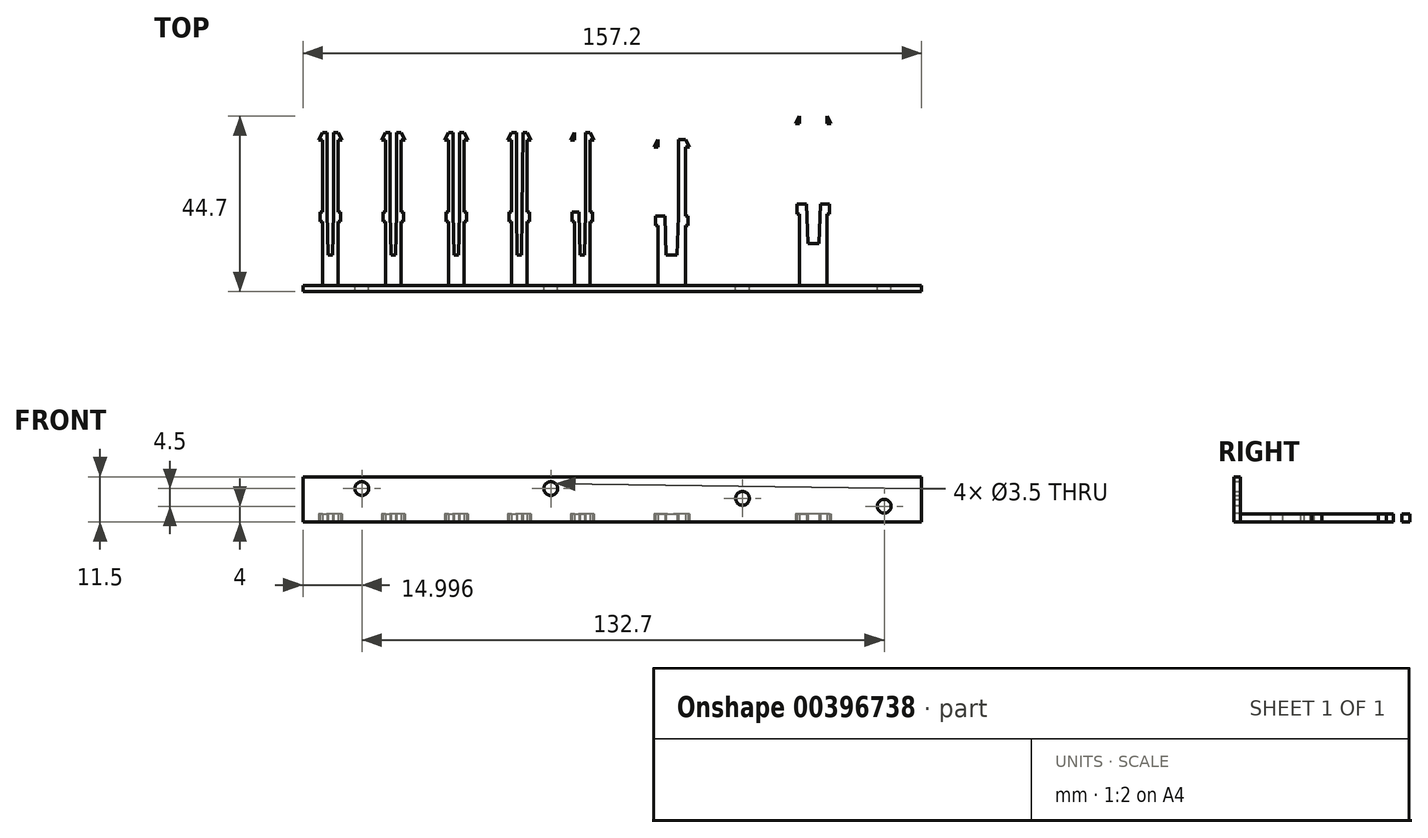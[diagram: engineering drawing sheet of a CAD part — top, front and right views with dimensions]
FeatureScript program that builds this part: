
annotation { "Feature Type Name" : "Feature", "Feature Type Description" : "" }
export const myFeature = defineFeature(function(context is Context, id is Id, definition is map)
    precondition{}
    {
        {
            var Q0;
            Q0=qCreatedBy(makeId("Top.planeOp"),FACE);
            var sketch = newSketch(context, id + "F0", { "sketchPlane" : qUnion([Q0])});
            skLineSegment(sketch, "E0.bottom", {"start": v(0.4, 5.8) * mm, "end": v(21.9, 5.8) * mm});
            skLineSegment(sketch, "E0.top", {"start": v(0.4, -4.9) * mm, "end": v(21.9, -4.9) * mm});
            skLineSegment(sketch, "E0.left", {"start": v(0.4, 5.8) * mm, "end": v(0.4, -4.9) * mm});
            skLineSegment(sketch, "E0.right", {"start": v(21.9, 5.8) * mm, "end": v(21.9, -4.9) * mm});
            skLineSegment(sketch, "E1.top", {"start": v(0.4, -7.9) * mm, "end": v(21.9, -7.9) * mm});
            skLineSegment(sketch, "E1.left", {"start": v(0.4, -4.9) * mm, "end": v(0.4, -7.9) * mm});
            skLineSegment(sketch, "E1.right", {"start": v(21.9, -4.9) * mm, "end": v(21.9, -7.9) * mm});
            skLineSegment(sketch, "E2.bottom", {"start": v(21.9, -7.9) * mm, "end": v(24.9, -7.9) * mm});
            skLineSegment(sketch, "E2.top", {"start": v(21.9, 8.8) * mm, "end": v(24.9, 8.8) * mm});
            skLineSegment(sketch, "E2.left", {"start": v(21.9, -7.9) * mm, "end": v(21.9, 8.8) * mm});
            skLineSegment(sketch, "E2.right", {"start": v(24.9, -7.9) * mm, "end": v(24.9, 8.8) * mm});
            skLineSegment(sketch, "E3", {"start": v(21.9, 8.8) * mm, "end": v(20.1, 5.8) * mm});
            skLineSegment(sketch, "E4.MirrorCS", {"start": v(0.4, -4.9) * mm, "end": v(-21.1, -4.9) * mm});
            skLineSegment(sketch, "E5.MirrorCS", {"start": v(-21.1, -7.9) * mm, "end": v(-21.1, 8.8) * mm});
            skLineSegment(sketch, "E6.MirrorCS", {"start": v(0.4, 5.8) * mm, "end": v(-21.1, 5.8) * mm});
            skLineSegment(sketch, "E7.MirrorCS", {"start": v(-21.1, 8.8) * mm, "end": v(-19.3, 5.8) * mm});
            skLineSegment(sketch, "E8.MirrorCS", {"start": v(-21.1, 8.8) * mm, "end": v(-24.1, 8.8) * mm});
            skLineSegment(sketch, "E9.MirrorCS", {"start": v(-24.1, -7.9) * mm, "end": v(-24.1, 8.8) * mm});
            skLineSegment(sketch, "E10.MirrorCS", {"start": v(0.4, -7.9) * mm, "end": v(-21.1, -7.9) * mm});
            skLineSegment(sketch, "E11.MirrorCS", {"start": v(-21.1, -7.9) * mm, "end": v(-24.1, -7.9) * mm});
            skLineSegment(sketch, "E12.bottom", {"start": v(0.4, -6.4) * mm, "end": v(3.4, -6.4) * mm});
            skLineSegment(sketch, "E12.top", {"start": v(0.4, -7.9) * mm, "end": v(3.4, -7.9) * mm});
            skLineSegment(sketch, "E12.left", {"start": v(0.4, -6.4) * mm, "end": v(0.4, -7.9) * mm});
            skLineSegment(sketch, "E12.right", {"start": v(3.4, -6.4) * mm, "end": v(3.4, -7.9) * mm});
            skLineSegment(sketch, "E13.MirrorCS", {"start": v(0.4, -6.4) * mm, "end": v(-2.6, -6.4) * mm});
            skLineSegment(sketch, "E14.MirrorCS", {"start": v(-2.6, -6.4) * mm, "end": v(-2.6, -7.9) * mm});
            skLineSegment(sketch, "E15.bottom", {"start": v(-24.1, -7.9) * mm, "end": v(-24.7, -7.9) * mm});
            skLineSegment(sketch, "E15.top", {"start": v(-24.1, -4.9) * mm, "end": v(-24.7, -4.9) * mm});
            skLineSegment(sketch, "E15.left", {"start": v(-24.1, -7.9) * mm, "end": v(-24.1, -4.9) * mm});
            skLineSegment(sketch, "E15.right", {"start": v(-24.7, -7.9) * mm, "end": v(-24.7, -4.9) * mm});
            skLineSegment(sketch, "E16.MirrorCS", {"start": v(-49.8, -4.9) * mm, "end": v(-49.8, -7.9) * mm});
            skLineSegment(sketch, "E17.MirrorCS", {"start": v(-49.8, -6.4) * mm, "end": v(-49.8, -7.9) * mm});
            skLineSegment(sketch, "E18.MirrorCS", {"start": v(-52.8, -6.4) * mm, "end": v(-52.8, -7.9) * mm});
            skLineSegment(sketch, "E19.MirrorCS", {"start": v(-46.8, -6.4) * mm, "end": v(-46.8, -7.9) * mm});
            skLineSegment(sketch, "E20.MirrorCS", {"start": v(-49.8, -4.9) * mm, "end": v(-71.3, -4.9) * mm});
            skLineSegment(sketch, "E21.MirrorCS", {"start": v(-71.3, 5.8) * mm, "end": v(-71.3, -4.9) * mm});
            skLineSegment(sketch, "E22.MirrorCS", {"start": v(-49.8, -6.4) * mm, "end": v(-52.8, -6.4) * mm});
            skLineSegment(sketch, "E23.MirrorCS", {"start": v(-71.3, -4.9) * mm, "end": v(-71.3, -7.9) * mm});
            skLineSegment(sketch, "E24.MirrorCS", {"start": v(-71.3, -7.9) * mm, "end": v(-74.3, -7.9) * mm});
            skLineSegment(sketch, "E25.MirrorCS", {"start": v(-49.8, -7.9) * mm, "end": v(-28.3, -7.9) * mm});
            skLineSegment(sketch, "E26.MirrorCS", {"start": v(-49.8, -7.9) * mm, "end": v(-52.8, -7.9) * mm});
            skLineSegment(sketch, "E27.MirrorCS", {"start": v(-49.8, -4.9) * mm, "end": v(-28.3, -4.9) * mm});
            skLineSegment(sketch, "E28.MirrorCS", {"start": v(-28.3, -7.9) * mm, "end": v(-28.3, 8.8) * mm});
            skLineSegment(sketch, "E29.MirrorCS", {"start": v(-49.8, 5.8) * mm, "end": v(-28.3, 5.8) * mm});
            skLineSegment(sketch, "E30.MirrorCS", {"start": v(-49.8, 5.8) * mm, "end": v(-71.3, 5.8) * mm});
            skLineSegment(sketch, "E31.MirrorCS", {"start": v(-28.3, 8.8) * mm, "end": v(-30.1, 5.8) * mm});
            skLineSegment(sketch, "E32.MirrorCS", {"start": v(-49.8, 5.8) * mm, "end": v(-49.8, -4.9) * mm});
            skLineSegment(sketch, "E33.MirrorCS", {"start": v(-49.8, -6.4) * mm, "end": v(-46.8, -6.4) * mm});
            skLineSegment(sketch, "E34.MirrorCS", {"start": v(-49.8, -7.9) * mm, "end": v(-71.3, -7.9) * mm});
            skLineSegment(sketch, "E35.MirrorCS", {"start": v(-28.3, -7.9) * mm, "end": v(-25.3, -7.9) * mm});
            skLineSegment(sketch, "E36.MirrorCS", {"start": v(-71.3, 8.8) * mm, "end": v(-74.3, 8.8) * mm});
            skLineSegment(sketch, "E37.MirrorCS", {"start": v(-71.3, -7.9) * mm, "end": v(-71.3, 8.8) * mm});
            skLineSegment(sketch, "E38.MirrorCS", {"start": v(-71.3, 8.8) * mm, "end": v(-69.5, 5.8) * mm});
            skLineSegment(sketch, "E39.MirrorCS", {"start": v(-28.3, 8.8) * mm, "end": v(-25.3, 8.8) * mm});
            skLineSegment(sketch, "E40.MirrorCS", {"start": v(-74.3, -7.9) * mm, "end": v(-74.3, 8.8) * mm});
            skLineSegment(sketch, "E41.MirrorCS", {"start": v(-25.3, -7.9) * mm, "end": v(-25.3, 8.8) * mm});
            skLineSegment(sketch, "E42.MirrorCS", {"start": v(-25.3, -4.9) * mm, "end": v(-24.7, -4.9) * mm});
            skLineSegment(sketch, "E43.MirrorCS", {"start": v(-25.3, -7.9) * mm, "end": v(-24.7, -7.9) * mm});
            skSolve(sketch);
        }
        {
            var Q0;
            Q0=qCreatedBy(makeId("Top.planeOp"),FACE);
            var sketch = newSketch(context, id + "F1", { "sketchPlane" : qUnion([Q0])});
            skLineSegment(sketch, "E44.bottom", {"start": v(-12.9, 18.7) * mm, "end": v(-10.9, 18.7) * mm});
            skLineSegment(sketch, "E44.top", {"start": v(-12.9, 0) * mm, "end": v(-10.9, 0) * mm});
            skLineSegment(sketch, "E44.left", {"start": v(-12.9, 18.7) * mm, "end": v(-12.9, 0) * mm});
            skLineSegment(sketch, "E44.right", {"start": v(-10.9, 18.7) * mm, "end": v(-10.9, 0) * mm});
            skLineSegment(sketch, "E45.bottom", {"start": v(-81.9, 0) * mm, "end": v(75.3, 0) * mm});
            skLineSegment(sketch, "E45.top", {"start": v(-81.9, -1.6) * mm, "end": v(75.3, -1.6) * mm});
            skLineSegment(sketch, "E45.left", {"start": v(-81.9, 0) * mm, "end": v(-81.9, -1.6) * mm});
            skLineSegment(sketch, "E45.right", {"start": v(75.3, 0) * mm, "end": v(75.3, -1.6) * mm});
            skLineSegment(sketch, "E46.top", {"start": v(-11.5, 7.7) * mm, "end": v(-10.9, 7.7) * mm});
            skLineSegment(sketch, "E47", {"start": v(-13.5, 16.2) * mm, "end": v(-12.9, 16.2) * mm});
            skLineSegment(sketch, "E48.MirrorCS", {"start": v(-10.3, 7.7) * mm, "end": v(-10.9, 7.7) * mm});
            skLineSegment(sketch, "E49.MirrorCS", {"start": v(-8.9, 18.7) * mm, "end": v(-8.9, 0) * mm});
            skLineSegment(sketch, "E50.MirrorCS", {"start": v(-8.3, 16.2) * mm, "end": v(-8.9, 16.2) * mm});
            skLineSegment(sketch, "E51.MirrorCS", {"start": v(-8.9, 18.7) * mm, "end": v(-10.9, 18.7) * mm});
            skLineSegment(sketch, "E52", {"start": v(-11.5, 7.7) * mm, "end": v(-11.7, 18.7) * mm});
            skLineSegment(sketch, "E53.MirrorCS", {"start": v(-10.3, 7.7) * mm, "end": v(-10.1, 18.7) * mm});
            skLineSegment(sketch, "E54.bottom", {"start": v(8.3, 17.7) * mm, "end": v(11.8, 17.7) * mm});
            skLineSegment(sketch, "E54.left", {"start": v(8.3, 17.7) * mm, "end": v(8.3, 0) * mm});
            skLineSegment(sketch, "E54.right", {"start": v(11.8, 17.7) * mm, "end": v(11.8, -1.3) * mm});
            skLineSegment(sketch, "E55.top", {"start": v(10.4, 7.7) * mm, "end": v(11.8, 7.7) * mm});
            skLineSegment(sketch, "E56", {"start": v(7.7, 15.2) * mm, "end": v(8.3, 15.2) * mm});
            skLineSegment(sketch, "E57.MirrorCS", {"start": v(13.2, 7.7) * mm, "end": v(11.8, 7.7) * mm});
            skLineSegment(sketch, "E58.MirrorCS", {"start": v(15.3, 17.7) * mm, "end": v(15.3, 0) * mm});
            skLineSegment(sketch, "E59.MirrorCS", {"start": v(15.9, 15.2) * mm, "end": v(15.3, 15.2) * mm});
            skLineSegment(sketch, "E60.MirrorCS", {"start": v(15.3, 17.7) * mm, "end": v(11.8, 17.7) * mm});
            skLineSegment(sketch, "E61", {"start": v(10.4, 7.7) * mm, "end": v(10.06, 17.7) * mm});
            skLineSegment(sketch, "E62.MirrorCS", {"start": v(13.2, 7.7) * mm, "end": v(13.56, 17.7) * mm});
            skLineSegment(sketch, "E63.bottom", {"start": v(44.3, 20.7) * mm, "end": v(47.8, 20.7) * mm});
            skLineSegment(sketch, "E63.left", {"start": v(44.3, 20.7) * mm, "end": v(44.3, 0) * mm});
            skLineSegment(sketch, "E63.right", {"start": v(47.8, 20.7) * mm, "end": v(47.8, -1.3) * mm});
            skLineSegment(sketch, "E64.top", {"start": v(46.4, 10.7) * mm, "end": v(47.8, 10.7) * mm});
            skLineSegment(sketch, "E65", {"start": v(43.7, 18.2) * mm, "end": v(44.3, 18.2) * mm});
            skLineSegment(sketch, "E66.MirrorCS", {"start": v(49.2, 10.7) * mm, "end": v(47.8, 10.7) * mm});
            skLineSegment(sketch, "E67.MirrorCS", {"start": v(51.3, 20.7) * mm, "end": v(51.3, 0) * mm});
            skLineSegment(sketch, "E68.MirrorCS", {"start": v(51.3, 20.7) * mm, "end": v(47.8, 20.7) * mm});
            skLineSegment(sketch, "E69", {"start": v(46.4, 10.7) * mm, "end": v(46.06, 20.7) * mm});
            skLineSegment(sketch, "E70.MirrorCS", {"start": v(49.2, 10.7) * mm, "end": v(49.56, 20.7) * mm});
            skLineSegment(sketch, "E71.top", {"start": v(-28.9, 0) * mm, "end": v(-26.9, 0) * mm});
            skLineSegment(sketch, "E71.left", {"start": v(-28.9, 18.7) * mm, "end": v(-28.9, 0) * mm});
            skLineSegment(sketch, "E71.right", {"start": v(-26.9, 18.7) * mm, "end": v(-26.9, 0) * mm});
            skLineSegment(sketch, "E72.top", {"start": v(-27.5, 7.7) * mm, "end": v(-26.9, 7.7) * mm});
            skLineSegment(sketch, "E73.MirrorCS", {"start": v(-26.3, 7.7) * mm, "end": v(-26.9, 7.7) * mm});
            skLineSegment(sketch, "E74.MirrorCS", {"start": v(-24.9, 18.7) * mm, "end": v(-24.9, 0) * mm});
            skLineSegment(sketch, "E75.MirrorCS", {"start": v(-24.3, 16.2) * mm, "end": v(-24.9, 16.2) * mm});
            skLineSegment(sketch, "E76.MirrorCS", {"start": v(-24.9, 18.7) * mm, "end": v(-26.9, 18.7) * mm});
            skLineSegment(sketch, "E77", {"start": v(-27.5, 7.7) * mm, "end": v(-27.64, 18.7) * mm});
            skLineSegment(sketch, "E78.MirrorCS", {"start": v(-26.3, 7.7) * mm, "end": v(-26.15, 18.7) * mm});
            skLineSegment(sketch, "E79.top", {"start": v(-44.9, 0) * mm, "end": v(-42.9, 0) * mm});
            skLineSegment(sketch, "E79.left", {"start": v(-44.9, 18.7) * mm, "end": v(-44.9, 0) * mm});
            skLineSegment(sketch, "E79.right", {"start": v(-42.9, 18.7) * mm, "end": v(-42.9, 0) * mm});
            skLineSegment(sketch, "E80.top", {"start": v(-43.5, 7.7) * mm, "end": v(-42.9, 7.7) * mm});
            skLineSegment(sketch, "E81", {"start": v(-45.5, 16.2) * mm, "end": v(-44.9, 16.2) * mm});
            skLineSegment(sketch, "E82.MirrorCS", {"start": v(-42.3, 7.7) * mm, "end": v(-42.9, 7.7) * mm});
            skLineSegment(sketch, "E83.MirrorCS", {"start": v(-40.9, 18.7) * mm, "end": v(-40.9, 0) * mm});
            skLineSegment(sketch, "E84.MirrorCS", {"start": v(-40.3, 16.2) * mm, "end": v(-40.9, 16.2) * mm});
            skLineSegment(sketch, "E85.MirrorCS", {"start": v(-40.9, 18.7) * mm, "end": v(-42.9, 18.7) * mm});
            skLineSegment(sketch, "E86", {"start": v(-43.5, 7.7) * mm, "end": v(-43.7, 18.7) * mm});
            skLineSegment(sketch, "E87.MirrorCS", {"start": v(-42.3, 7.7) * mm, "end": v(-42.1, 18.7) * mm});
            skLineSegment(sketch, "E88.top", {"start": v(-60.9, 0) * mm, "end": v(-58.9, 0) * mm});
            skLineSegment(sketch, "E88.left", {"start": v(-60.9, 18.7) * mm, "end": v(-60.9, 0) * mm});
            skLineSegment(sketch, "E88.right", {"start": v(-58.9, 18.7) * mm, "end": v(-58.9, 0) * mm});
            skLineSegment(sketch, "E89.top", {"start": v(-59.5, 7.7) * mm, "end": v(-58.9, 7.7) * mm});
            skLineSegment(sketch, "E90", {"start": v(-61.5, 16.2) * mm, "end": v(-60.9, 16.2) * mm});
            skLineSegment(sketch, "E91.MirrorCS", {"start": v(-58.3, 7.7) * mm, "end": v(-58.9, 7.7) * mm});
            skLineSegment(sketch, "E92.MirrorCS", {"start": v(-56.9, 18.7) * mm, "end": v(-56.9, 0) * mm});
            skLineSegment(sketch, "E93.MirrorCS", {"start": v(-56.3, 16.2) * mm, "end": v(-56.9, 16.2) * mm});
            skLineSegment(sketch, "E94.MirrorCS", {"start": v(-56.9, 18.7) * mm, "end": v(-58.9, 18.7) * mm});
            skLineSegment(sketch, "E95", {"start": v(-59.5, 7.7) * mm, "end": v(-59.7, 18.7) * mm});
            skLineSegment(sketch, "E96.MirrorCS", {"start": v(-58.3, 7.7) * mm, "end": v(-58.1, 18.7) * mm});
            skLineSegment(sketch, "E97.top", {"start": v(-76.9, 0) * mm, "end": v(-74.9, 0) * mm});
            skLineSegment(sketch, "E97.left", {"start": v(-76.9, 18.7) * mm, "end": v(-76.9, 0) * mm});
            skLineSegment(sketch, "E97.right", {"start": v(-74.9, 18.7) * mm, "end": v(-74.9, 0) * mm});
            skLineSegment(sketch, "E98.top", {"start": v(-75.5, 7.7) * mm, "end": v(-74.9, 7.7) * mm});
            skLineSegment(sketch, "E99", {"start": v(-77.5, 16.2) * mm, "end": v(-76.9, 16.2) * mm});
            skLineSegment(sketch, "E100.MirrorCS", {"start": v(-74.3, 7.7) * mm, "end": v(-74.9, 7.7) * mm});
            skLineSegment(sketch, "E101.MirrorCS", {"start": v(-72.9, 18.7) * mm, "end": v(-72.9, 0) * mm});
            skLineSegment(sketch, "E102.MirrorCS", {"start": v(-72.3, 16.2) * mm, "end": v(-72.9, 16.2) * mm});
            skLineSegment(sketch, "E103.MirrorCS", {"start": v(-72.9, 18.7) * mm, "end": v(-74.9, 18.7) * mm});
            skLineSegment(sketch, "E104", {"start": v(-75.5, 7.7) * mm, "end": v(-75.7, 18.7) * mm});
            skLineSegment(sketch, "E105.MirrorCS", {"start": v(-74.3, 7.7) * mm, "end": v(-74.1, 18.7) * mm});
            skLineSegment(sketch, "E106.bottom", {"start": v(44.3, 20.7) * mm, "end": v(46.06, 20.7) * mm});
            skLineSegment(sketch, "E106.top", {"start": v(44.3, 43.1) * mm, "end": v(46.06, 43.1) * mm});
            skLineSegment(sketch, "E106.left", {"start": v(44.3, 20.7) * mm, "end": v(44.3, 43.1) * mm});
            skLineSegment(sketch, "E106.right", {"start": v(46.06, 20.7) * mm, "end": v(46.06, 43.1) * mm});
            skLineSegment(sketch, "E107.bottom", {"start": v(51.3, 20.7) * mm, "end": v(49.56, 20.7) * mm});
            skLineSegment(sketch, "E108", {"start": v(44.3, 41.1) * mm, "end": v(43.3, 41.1) * mm});
            skLineSegment(sketch, "E109", {"start": v(43.3, 41.1) * mm, "end": v(44.3, 43.1) * mm});
            skLineSegment(sketch, "E110.top", {"start": v(43.7, 20.7) * mm, "end": v(44.3, 20.7) * mm});
            skLineSegment(sketch, "E110.left", {"start": v(43.7, 18.2) * mm, "end": v(43.7, 20.7) * mm});
            skLineSegment(sketch, "E110.right", {"start": v(44.3, 18.2) * mm, "end": v(44.3, 20.7) * mm});
            skLineSegment(sketch, "E111.MirrorCS", {"start": v(51.9, 18.2) * mm, "end": v(51.3, 18.2) * mm});
            skLineSegment(sketch, "E112.MirrorCS", {"start": v(51.9, 18.2) * mm, "end": v(51.9, 20.7) * mm});
            skLineSegment(sketch, "E113.MirrorCS", {"start": v(51.9, 20.7) * mm, "end": v(51.3, 20.7) * mm});
            skLineSegment(sketch, "E114.MirrorCS", {"start": v(51.3, 20.7) * mm, "end": v(51.3, 43.1) * mm});
            skLineSegment(sketch, "E115.MirrorCS", {"start": v(49.56, 20.7) * mm, "end": v(49.56, 43.1) * mm});
            skLineSegment(sketch, "E116.MirrorCS", {"start": v(51.3, 41.1) * mm, "end": v(52.3, 41.1) * mm});
            skLineSegment(sketch, "E117.MirrorCS", {"start": v(52.3, 41.1) * mm, "end": v(51.3, 43.1) * mm});
            skLineSegment(sketch, "E118.MirrorCS", {"start": v(51.3, 43.1) * mm, "end": v(49.56, 43.1) * mm});
            skLineSegment(sketch, "E119.top", {"start": v(7.7, 17.7) * mm, "end": v(8.3, 17.7) * mm});
            skLineSegment(sketch, "E119.left", {"start": v(7.7, 15.2) * mm, "end": v(7.7, 17.7) * mm});
            skLineSegment(sketch, "E119.right", {"start": v(8.3, 15.2) * mm, "end": v(8.3, 17.7) * mm});
            skLineSegment(sketch, "E120.bottom", {"start": v(8.3, 17.7) * mm, "end": v(10.06, 17.7) * mm});
            skLineSegment(sketch, "E120.top", {"start": v(8.3, 37.1) * mm, "end": v(10.06, 37.1) * mm});
            skLineSegment(sketch, "E120.left", {"start": v(8.3, 17.7) * mm, "end": v(8.3, 37.1) * mm});
            skLineSegment(sketch, "E120.right", {"start": v(10.06, 17.7) * mm, "end": v(10.06, 37.1) * mm});
            skLineSegment(sketch, "E121", {"start": v(8.3, 37.1) * mm, "end": v(7.3, 35.1) * mm});
            skLineSegment(sketch, "E122", {"start": v(7.3, 35.1) * mm, "end": v(8.3, 35.1) * mm});
            skLineSegment(sketch, "E123.MirrorCS", {"start": v(13.56, 17.7) * mm, "end": v(13.56, 37.1) * mm});
            skLineSegment(sketch, "E124.MirrorCS", {"start": v(15.3, 17.7) * mm, "end": v(15.3, 37.1) * mm});
            skLineSegment(sketch, "E125.MirrorCS", {"start": v(15.3, 37.1) * mm, "end": v(13.56, 37.1) * mm});
            skLineSegment(sketch, "E126.MirrorCS", {"start": v(15.3, 37.1) * mm, "end": v(16.3, 35.1) * mm});
            skLineSegment(sketch, "E127.MirrorCS", {"start": v(16.3, 35.1) * mm, "end": v(15.3, 35.1) * mm});
            skLineSegment(sketch, "E128.MirrorCS", {"start": v(15.9, 17.7) * mm, "end": v(15.3, 17.7) * mm});
            skLineSegment(sketch, "E129.MirrorCS", {"start": v(15.9, 15.2) * mm, "end": v(15.9, 17.7) * mm});
            skLineSegment(sketch, "E130.top", {"start": v(-13.5, 18.7) * mm, "end": v(-12.9, 18.7) * mm});
            skLineSegment(sketch, "E130.left", {"start": v(-13.5, 16.2) * mm, "end": v(-13.5, 18.7) * mm});
            skLineSegment(sketch, "E130.right", {"start": v(-12.9, 16.2) * mm, "end": v(-12.9, 18.7) * mm});
            skLineSegment(sketch, "E131.bottom", {"start": v(-12.9, 18.7) * mm, "end": v(-11.9, 18.7) * mm});
            skLineSegment(sketch, "E131.top", {"start": v(-12.9, 38.9) * mm, "end": v(-11.7, 38.9) * mm});
            skLineSegment(sketch, "E131.left", {"start": v(-12.9, 18.7) * mm, "end": v(-12.9, 38.9) * mm});
            skLineSegment(sketch, "E131.right", {"start": v(-11.7, 18.7) * mm, "end": v(-11.7, 38.9) * mm});
            skLineSegment(sketch, "E132", {"start": v(-12.9, 38.9) * mm, "end": v(-13.9, 36.9) * mm});
            skLineSegment(sketch, "E133", {"start": v(-13.9, 36.9) * mm, "end": v(-12.9, 36.9) * mm});
            skLineSegment(sketch, "E134.MirrorCS", {"start": v(-8.3, 18.7) * mm, "end": v(-8.9, 18.7) * mm});
            skLineSegment(sketch, "E135.MirrorCS", {"start": v(-8.3, 16.2) * mm, "end": v(-8.3, 18.7) * mm});
            skLineSegment(sketch, "E136.MirrorCS", {"start": v(-10.1, 18.7) * mm, "end": v(-10.1, 38.9) * mm});
            skLineSegment(sketch, "E137.MirrorCS", {"start": v(-8.9, 18.7) * mm, "end": v(-8.9, 38.9) * mm});
            skLineSegment(sketch, "E138.MirrorCS", {"start": v(-7.9, 36.9) * mm, "end": v(-8.9, 36.9) * mm});
            skLineSegment(sketch, "E139.MirrorCS", {"start": v(-8.9, 38.9) * mm, "end": v(-7.9, 36.9) * mm});
            skLineSegment(sketch, "E140.MirrorCS", {"start": v(-8.9, 38.9) * mm, "end": v(-10.1, 38.9) * mm});
            skLineSegment(sketch, "E141.MirrorCS", {"start": v(-29.5, 16.2) * mm, "end": v(-28.9, 16.2) * mm});
            skLineSegment(sketch, "E142.left", {"start": v(-29.5, 16.2) * mm, "end": v(-29.5, 18.7) * mm});
            skLineSegment(sketch, "E143.top", {"start": v(-28.9, 38.9) * mm, "end": v(-27.64, 38.9) * mm});
            skLineSegment(sketch, "E143.left", {"start": v(-28.9, 18.7) * mm, "end": v(-28.9, 38.9) * mm});
            skLineSegment(sketch, "E143.right", {"start": v(-27.64, 18.7) * mm, "end": v(-27.64, 38.9) * mm});
            skLineSegment(sketch, "E144", {"start": v(-28.9, 38.9) * mm, "end": v(-29.9, 36.9) * mm});
            skLineSegment(sketch, "E145", {"start": v(-29.9, 36.9) * mm, "end": v(-28.9, 36.9) * mm});
            skLineSegment(sketch, "E146.MirrorCS", {"start": v(-24.3, 18.7) * mm, "end": v(-24.9, 18.7) * mm});
            skLineSegment(sketch, "E147.MirrorCS", {"start": v(-24.3, 16.2) * mm, "end": v(-24.3, 18.7) * mm});
            skLineSegment(sketch, "E148.MirrorCS", {"start": v(-26.15, 18.7) * mm, "end": v(-25.9, 38.9) * mm});
            skLineSegment(sketch, "E149.MirrorCS", {"start": v(-24.9, 18.7) * mm, "end": v(-24.9, 38.9) * mm});
            skLineSegment(sketch, "E150.MirrorCS", {"start": v(-23.9, 36.9) * mm, "end": v(-24.9, 36.9) * mm});
            skLineSegment(sketch, "E151.MirrorCS", {"start": v(-24.9, 38.9) * mm, "end": v(-23.9, 36.9) * mm});
            skLineSegment(sketch, "E152.MirrorCS", {"start": v(-24.9, 38.9) * mm, "end": v(-25.9, 38.9) * mm});
            skLineSegment(sketch, "E153.left", {"start": v(-45.5, 16.2) * mm, "end": v(-45.5, 18.7) * mm});
            skLineSegment(sketch, "E154.top", {"start": v(-44.9, 38.9) * mm, "end": v(-43.7, 38.9) * mm});
            skLineSegment(sketch, "E154.left", {"start": v(-44.9, 18.7) * mm, "end": v(-44.9, 38.9) * mm});
            skLineSegment(sketch, "E154.right", {"start": v(-43.7, 18.7) * mm, "end": v(-43.7, 38.9) * mm});
            skLineSegment(sketch, "E155", {"start": v(-44.9, 38.9) * mm, "end": v(-45.9, 36.9) * mm});
            skLineSegment(sketch, "E156", {"start": v(-45.9, 36.9) * mm, "end": v(-44.9, 36.9) * mm});
            skLineSegment(sketch, "E157.MirrorCS", {"start": v(-40.3, 18.7) * mm, "end": v(-40.9, 18.7) * mm});
            skLineSegment(sketch, "E158.MirrorCS", {"start": v(-40.3, 16.2) * mm, "end": v(-40.3, 18.7) * mm});
            skLineSegment(sketch, "E159.MirrorCS", {"start": v(-40.9, 18.7) * mm, "end": v(-40.9, 38.9) * mm});
            skLineSegment(sketch, "E160.MirrorCS", {"start": v(-39.9, 36.9) * mm, "end": v(-40.9, 36.9) * mm});
            skLineSegment(sketch, "E161.MirrorCS", {"start": v(-40.9, 38.9) * mm, "end": v(-39.9, 36.9) * mm});
            skLineSegment(sketch, "E162.top", {"start": v(-61.5, 18.7) * mm, "end": v(-60.9, 18.7) * mm});
            skLineSegment(sketch, "E162.left", {"start": v(-61.5, 16.2) * mm, "end": v(-61.5, 18.7) * mm});
            skLineSegment(sketch, "E163.top", {"start": v(-60.9, 38.9) * mm, "end": v(-59.7, 38.9) * mm});
            skLineSegment(sketch, "E163.left", {"start": v(-60.9, 18.7) * mm, "end": v(-60.9, 38.9) * mm});
            skLineSegment(sketch, "E163.right", {"start": v(-59.7, 18.7) * mm, "end": v(-59.7, 38.9) * mm});
            skLineSegment(sketch, "E164", {"start": v(-60.9, 38.9) * mm, "end": v(-61.9, 36.9) * mm});
            skLineSegment(sketch, "E165", {"start": v(-61.9, 36.9) * mm, "end": v(-60.9, 36.9) * mm});
            skLineSegment(sketch, "E166.MirrorCS", {"start": v(-56.3, 18.7) * mm, "end": v(-56.9, 18.7) * mm});
            skLineSegment(sketch, "E167.MirrorCS", {"start": v(-56.3, 16.2) * mm, "end": v(-56.3, 18.7) * mm});
            skLineSegment(sketch, "E168.MirrorCS", {"start": v(-56.9, 18.7) * mm, "end": v(-56.9, 38.9) * mm});
            skLineSegment(sketch, "E169.MirrorCS", {"start": v(-55.9, 36.9) * mm, "end": v(-56.9, 36.9) * mm});
            skLineSegment(sketch, "E170.MirrorCS", {"start": v(-56.9, 38.9) * mm, "end": v(-55.9, 36.9) * mm});
            skLineSegment(sketch, "E171.top", {"start": v(-77.5, 18.7) * mm, "end": v(-76.9, 18.7) * mm});
            skLineSegment(sketch, "E171.left", {"start": v(-77.5, 16.2) * mm, "end": v(-77.5, 18.7) * mm});
            skLineSegment(sketch, "E172.top", {"start": v(-76.9, 38.9) * mm, "end": v(-75.7, 38.9) * mm});
            skLineSegment(sketch, "E172.left", {"start": v(-76.9, 18.7) * mm, "end": v(-76.9, 38.9) * mm});
            skLineSegment(sketch, "E172.right", {"start": v(-75.7, 18.7) * mm, "end": v(-75.7, 38.9) * mm});
            skLineSegment(sketch, "E173", {"start": v(-76.9, 38.9) * mm, "end": v(-77.9, 36.9) * mm});
            skLineSegment(sketch, "E174", {"start": v(-77.9, 36.9) * mm, "end": v(-76.9, 36.9) * mm});
            skLineSegment(sketch, "E175.MirrorCS", {"start": v(-72.3, 18.7) * mm, "end": v(-72.9, 18.7) * mm});
            skLineSegment(sketch, "E176.MirrorCS", {"start": v(-72.3, 16.2) * mm, "end": v(-72.3, 18.7) * mm});
            skLineSegment(sketch, "E177.MirrorCS", {"start": v(-72.9, 18.7) * mm, "end": v(-72.9, 38.9) * mm});
            skLineSegment(sketch, "E178.MirrorCS", {"start": v(-71.9, 36.9) * mm, "end": v(-72.9, 36.9) * mm});
            skLineSegment(sketch, "E179.MirrorCS", {"start": v(-72.9, 38.9) * mm, "end": v(-71.9, 36.9) * mm});
            skLineSegment(sketch, "E180", {"start": v(-29.5, 18.7) * mm, "end": v(-28.9, 18.7) * mm});
            skLineSegment(sketch, "E181.MirrorCS", {"start": v(-42.1, 18.7) * mm, "end": v(-42.1, 38.9) * mm});
            skLineSegment(sketch, "E182.MirrorCS", {"start": v(-40.9, 38.9) * mm, "end": v(-42.1, 38.9) * mm});
            skLineSegment(sketch, "E183", {"start": v(-45.5, 18.7) * mm, "end": v(-44.9, 18.7) * mm});
            skLineSegment(sketch, "E184.MirrorCS", {"start": v(-74.1, 18.7) * mm, "end": v(-74.1, 38.9) * mm});
            skLineSegment(sketch, "E185.MirrorCS", {"start": v(-72.9, 38.9) * mm, "end": v(-74.1, 38.9) * mm});
            skLineSegment(sketch, "E186.MirrorCS", {"start": v(-58.1, 18.7) * mm, "end": v(-58.1, 38.9) * mm});
            skLineSegment(sketch, "E187.MirrorCS", {"start": v(-56.9, 38.9) * mm, "end": v(-58.1, 38.9) * mm});
            skSolve(sketch);
        }
        {
            var Q0;
            {var subQ2=sQuery(id+"F1.wireOp",EDGE,"E47");Q0=makeQuery(id+"F1.imprint","IMPRINT",FACE,{"disambiguationData":[TD([[makeQuery(id+"F1.imprint","IMPRINT",EDGE,{"derivedFrom":subQ2}),1.0]])]});}
            var Q1;
            {var subQ8=sQuery(id+"F1.wireOp",EDGE,"E46.top");Q1=makeQuery(id+"F1.imprint","IMPRINT",FACE,{"disambiguationData":[TD([[makeQuery(id+"F1.imprint","IMPRINT",EDGE,{"derivedFrom":subQ8}),-1.0]])]});}
            var Q2;
            {var subQ0=sQuery(id+"F1.wireOp",EDGE,"E48.MirrorCS");Q2=makeQuery(id+"F1.imprint","IMPRINT",FACE,{"disambiguationData":[TD([[makeQuery(id+"F1.imprint","IMPRINT",EDGE,{"derivedFrom":subQ0}),1.0]])]});}
            var Q3;
            {var subQ2=sQuery(id+"F1.wireOp",EDGE,"E50.MirrorCS");Q3=makeQuery(id+"F1.imprint","IMPRINT",FACE,{"disambiguationData":[TD([[makeQuery(id+"F1.imprint","IMPRINT",EDGE,{"derivedFrom":subQ2}),-1.0]])]});}
            var Q4;
            {var subQ2=sQuery(id+"F1.wireOp",EDGE,"E59.MirrorCS");Q4=makeQuery(id+"F1.imprint","IMPRINT",FACE,{"disambiguationData":[TD([[makeQuery(id+"F1.imprint","IMPRINT",EDGE,{"derivedFrom":subQ2}),-1.0]])]});}
            var Q5;
            {var subQ2=sQuery(id+"F1.wireOp",EDGE,"E56");Q5=makeQuery(id+"F1.imprint","IMPRINT",FACE,{"disambiguationData":[TD([[makeQuery(id+"F1.imprint","IMPRINT",EDGE,{"derivedFrom":subQ2}),1.0]])]});}
            var Q6;
            {var subQ9=sQuery(id+"F1.wireOp",EDGE,"E55.top");Q6=makeQuery(id+"F1.imprint","IMPRINT",FACE,{"disambiguationData":[TD([[makeQuery(id+"F1.imprint","IMPRINT",EDGE,{"derivedFrom":subQ9}),-1.0]])]});}
            var Q7;
            {var subQ8=sQuery(id+"F1.wireOp",EDGE,"E57.MirrorCS");Q7=makeQuery(id+"F1.imprint","IMPRINT",FACE,{"disambiguationData":[TD([[makeQuery(id+"F1.imprint","IMPRINT",EDGE,{"derivedFrom":subQ8}),1.0]])]});}
            var Q8;
            {var subQ0=sQuery(id+"F1.wireOp",EDGE,"E45.bottom");var subQ9=makeQuery(id+"F1.imprint","INTERSECT",VERTEX,{"derivedFrom":[subQ0,sQuery(id+"F1.wireOp",EDGE,"E58.MirrorCS")]});Q8=makeQuery(id+"F1.imprint","IMPRINT",FACE,{"disambiguationData":[TD([[makeQuery(id+"F1.imprint","IMPRINT",EDGE,{"disambiguationData":[TD([[subQ9,1.0]])],"derivedFrom":subQ0}),-1.0]])]});}
            var Q9;
            {var subQ4=sQuery(id+"F1.wireOp",EDGE,"E45.left");Q9=makeQuery(id+"F1.imprint","IMPRINT",FACE,{"disambiguationData":[TD([[makeQuery(id+"F1.imprint","IMPRINT",EDGE,{"derivedFrom":subQ4}),1.0]])]});}
            var Q10;
            {var subQ0=sQuery(id+"F1.wireOp",EDGE,"E45.right");Q10=makeQuery(id+"F1.imprint","IMPRINT",FACE,{"disambiguationData":[TD([[makeQuery(id+"F1.imprint","IMPRINT",EDGE,{"derivedFrom":subQ0}),-1.0]])]});}
            var Q11;
            {var subQ4=sQuery(id+"F1.wireOp",EDGE,"E66.MirrorCS");Q11=makeQuery(id+"F1.imprint","IMPRINT",FACE,{"disambiguationData":[TD([[makeQuery(id+"F1.imprint","IMPRINT",EDGE,{"derivedFrom":subQ4}),1.0]])]});}
            var Q12;
            {var subQ9=sQuery(id+"F1.wireOp",EDGE,"E64.top");Q12=makeQuery(id+"F1.imprint","IMPRINT",FACE,{"disambiguationData":[TD([[makeQuery(id+"F1.imprint","IMPRINT",EDGE,{"derivedFrom":subQ9}),-1.0]])]});}
            var Q13;
            {var subQ2=sQuery(id+"F1.wireOp",EDGE,"3d1c4982-7607-47c5-8404-859363080553.MirrorCS");Q13=makeQuery(id+"F1.imprint","IMPRINT",FACE,{"disambiguationData":[TD([[makeQuery(id+"F1.imprint","IMPRINT",EDGE,{"derivedFrom":subQ2}),-1.0]])]});}
            var Q14;
            {var subQ2=sQuery(id+"F1.wireOp",EDGE,"E65");Q14=makeQuery(id+"F1.imprint","IMPRINT",FACE,{"disambiguationData":[TD([[makeQuery(id+"F1.imprint","IMPRINT",EDGE,{"derivedFrom":subQ2}),1.0]])]});}
            var Q15;
            {var subQ0=sQuery(id+"F1.wireOp",EDGE,"E73.MirrorCS");Q15=makeQuery(id+"F1.imprint","IMPRINT",FACE,{"disambiguationData":[TD([[makeQuery(id+"F1.imprint","IMPRINT",EDGE,{"derivedFrom":subQ0}),1.0]])]});}
            var Q16;
            {var subQ1=sQuery(id+"F1.wireOp",EDGE,"E71.top");Q16=makeQuery(id+"F1.imprint","IMPRINT",FACE,{"disambiguationData":[TD([[makeQuery(id+"F1.imprint","IMPRINT",EDGE,{"derivedFrom":subQ1}),1.0]])]});}
            var Q17;
            {var subQ2=sQuery(id+"F1.wireOp",EDGE,"26c9bbb3-c2e7-476d-81d8-3d66ad1d6840");Q17=makeQuery(id+"F1.imprint","IMPRINT",FACE,{"disambiguationData":[TD([[makeQuery(id+"F1.imprint","IMPRINT",EDGE,{"derivedFrom":subQ2}),1.0]])]});}
            var Q18;
            {var subQ2=sQuery(id+"F1.wireOp",EDGE,"E75.MirrorCS");Q18=makeQuery(id+"F1.imprint","IMPRINT",FACE,{"disambiguationData":[TD([[makeQuery(id+"F1.imprint","IMPRINT",EDGE,{"derivedFrom":subQ2}),-1.0]])]});}
            var Q19;
            {var subQ2=sQuery(id+"F1.wireOp",EDGE,"E84.MirrorCS");Q19=makeQuery(id+"F1.imprint","IMPRINT",FACE,{"disambiguationData":[TD([[makeQuery(id+"F1.imprint","IMPRINT",EDGE,{"derivedFrom":subQ2}),-1.0]])]});}
            var Q20;
            {var subQ2=sQuery(id+"F1.wireOp",EDGE,"E81");Q20=makeQuery(id+"F1.imprint","IMPRINT",FACE,{"disambiguationData":[TD([[makeQuery(id+"F1.imprint","IMPRINT",EDGE,{"derivedFrom":subQ2}),1.0]])]});}
            var Q21;
            {var subQ1=sQuery(id+"F1.wireOp",EDGE,"E79.top");Q21=makeQuery(id+"F1.imprint","IMPRINT",FACE,{"disambiguationData":[TD([[makeQuery(id+"F1.imprint","IMPRINT",EDGE,{"derivedFrom":subQ1}),1.0]])]});}
            var Q22;
            {var subQ0=sQuery(id+"F1.wireOp",EDGE,"E82.MirrorCS");Q22=makeQuery(id+"F1.imprint","IMPRINT",FACE,{"disambiguationData":[TD([[makeQuery(id+"F1.imprint","IMPRINT",EDGE,{"derivedFrom":subQ0}),1.0]])]});}
            var Q23;
            {var subQ0=sQuery(id+"F1.wireOp",EDGE,"E91.MirrorCS");Q23=makeQuery(id+"F1.imprint","IMPRINT",FACE,{"disambiguationData":[TD([[makeQuery(id+"F1.imprint","IMPRINT",EDGE,{"derivedFrom":subQ0}),1.0]])]});}
            var Q24;
            {var subQ1=sQuery(id+"F1.wireOp",EDGE,"E88.top");Q24=makeQuery(id+"F1.imprint","IMPRINT",FACE,{"disambiguationData":[TD([[makeQuery(id+"F1.imprint","IMPRINT",EDGE,{"derivedFrom":subQ1}),1.0]])]});}
            var Q25;
            {var subQ2=sQuery(id+"F1.wireOp",EDGE,"E93.MirrorCS");Q25=makeQuery(id+"F1.imprint","IMPRINT",FACE,{"disambiguationData":[TD([[makeQuery(id+"F1.imprint","IMPRINT",EDGE,{"derivedFrom":subQ2}),-1.0]])]});}
            var Q26;
            {var subQ2=sQuery(id+"F1.wireOp",EDGE,"E90");Q26=makeQuery(id+"F1.imprint","IMPRINT",FACE,{"disambiguationData":[TD([[makeQuery(id+"F1.imprint","IMPRINT",EDGE,{"derivedFrom":subQ2}),1.0]])]});}
            var Q27;
            {var subQ7=sQuery(id+"F1.wireOp",EDGE,"E100.MirrorCS");Q27=makeQuery(id+"F1.imprint","IMPRINT",FACE,{"disambiguationData":[TD([[makeQuery(id+"F1.imprint","IMPRINT",EDGE,{"derivedFrom":subQ7}),1.0]])]});}
            var Q28;
            {var subQ2=sQuery(id+"F1.wireOp",EDGE,"E102.MirrorCS");Q28=makeQuery(id+"F1.imprint","IMPRINT",FACE,{"disambiguationData":[TD([[makeQuery(id+"F1.imprint","IMPRINT",EDGE,{"derivedFrom":subQ2}),-1.0]])]});}
            var Q29;
            {var subQ2=sQuery(id+"F1.wireOp",EDGE,"E99");Q29=makeQuery(id+"F1.imprint","IMPRINT",FACE,{"disambiguationData":[TD([[makeQuery(id+"F1.imprint","IMPRINT",EDGE,{"derivedFrom":subQ2}),1.0]])]});}
            var Q30;
            {var subQ1=sQuery(id+"F1.wireOp",EDGE,"E97.top");Q30=makeQuery(id+"F1.imprint","IMPRINT",FACE,{"disambiguationData":[TD([[makeQuery(id+"F1.imprint","IMPRINT",EDGE,{"derivedFrom":subQ1}),1.0]])]});}
            var Q31;
            {var subQ2=sQuery(id+"F1.wireOp",EDGE,"E178.MirrorCS");Q31=makeQuery(id+"F1.imprint","IMPRINT",FACE,{"disambiguationData":[TD([[makeQuery(id+"F1.imprint","IMPRINT",EDGE,{"derivedFrom":subQ2}),-1.0]])]});}
            var Q32;
            {var subQ5=sQuery(id+"F1.wireOp",EDGE,"b1517702-5842-47e0-8168-d100c116fc8b.MirrorCS");Q32=makeQuery(id+"F1.imprint","IMPRINT",FACE,{"disambiguationData":[TD([[makeQuery(id+"F1.imprint","IMPRINT",EDGE,{"derivedFrom":subQ5}),-1.0]])]});}
            var Q33;
            {var subQ1=sQuery(id+"F1.wireOp",EDGE,"E172.top");Q33=makeQuery(id+"F1.imprint","IMPRINT",FACE,{"disambiguationData":[TD([[makeQuery(id+"F1.imprint","IMPRINT",EDGE,{"derivedFrom":subQ1}),-1.0]])]});}
            var Q34;
            {var subQ0=sQuery(id+"F1.wireOp",EDGE,"E173");Q34=makeQuery(id+"F1.imprint","IMPRINT",FACE,{"disambiguationData":[TD([[makeQuery(id+"F1.imprint","IMPRINT",EDGE,{"derivedFrom":subQ0}),1.0]])]});}
            var Q35;
            {var subQ0=sQuery(id+"F1.wireOp",EDGE,"E164");Q35=makeQuery(id+"F1.imprint","IMPRINT",FACE,{"disambiguationData":[TD([[makeQuery(id+"F1.imprint","IMPRINT",EDGE,{"derivedFrom":subQ0}),1.0]])]});}
            var Q36;
            {var subQ4=sQuery(id+"F1.wireOp",EDGE,"E163.top");Q36=makeQuery(id+"F1.imprint","IMPRINT",FACE,{"disambiguationData":[TD([[makeQuery(id+"F1.imprint","IMPRINT",EDGE,{"derivedFrom":subQ4}),-1.0]])]});}
            var Q37;
            {var subQ4=sQuery(id+"F1.wireOp",EDGE,"4252b33a-d792-468b-8066-8b175ecf75e6.MirrorCS");Q37=makeQuery(id+"F1.imprint","IMPRINT",FACE,{"disambiguationData":[TD([[makeQuery(id+"F1.imprint","IMPRINT",EDGE,{"derivedFrom":subQ4}),-1.0]])]});}
            var Q38;
            {var subQ0=sQuery(id+"F1.wireOp",EDGE,"E155");Q38=makeQuery(id+"F1.imprint","IMPRINT",FACE,{"disambiguationData":[TD([[makeQuery(id+"F1.imprint","IMPRINT",EDGE,{"derivedFrom":subQ0}),1.0]])]});}
            var Q39;
            {var subQ1=sQuery(id+"F1.wireOp",EDGE,"E154.top");Q39=makeQuery(id+"F1.imprint","IMPRINT",FACE,{"disambiguationData":[TD([[makeQuery(id+"F1.imprint","IMPRINT",EDGE,{"derivedFrom":subQ1}),-1.0]])]});}
            var Q40;
            {var subQ2=sQuery(id+"F1.wireOp",EDGE,"E160.MirrorCS");Q40=makeQuery(id+"F1.imprint","IMPRINT",FACE,{"disambiguationData":[TD([[makeQuery(id+"F1.imprint","IMPRINT",EDGE,{"derivedFrom":subQ2}),-1.0]])]});}
            var Q41;
            {var subQ0=sQuery(id+"F1.wireOp",EDGE,"E144");Q41=makeQuery(id+"F1.imprint","IMPRINT",FACE,{"disambiguationData":[TD([[makeQuery(id+"F1.imprint","IMPRINT",EDGE,{"derivedFrom":subQ0}),1.0]])]});}
            var Q42;
            {var subQ1=sQuery(id+"F1.wireOp",EDGE,"E143.top");Q42=makeQuery(id+"F1.imprint","IMPRINT",FACE,{"disambiguationData":[TD([[makeQuery(id+"F1.imprint","IMPRINT",EDGE,{"derivedFrom":subQ1}),-1.0]])]});}
            var Q43;
            {var subQ5=sQuery(id+"F1.wireOp",EDGE,"E148.MirrorCS");Q43=makeQuery(id+"F1.imprint","IMPRINT",FACE,{"disambiguationData":[TD([[makeQuery(id+"F1.imprint","IMPRINT",EDGE,{"derivedFrom":subQ5}),-1.0]])]});}
            var Q44;
            {var subQ2=sQuery(id+"F1.wireOp",EDGE,"E150.MirrorCS");Q44=makeQuery(id+"F1.imprint","IMPRINT",FACE,{"disambiguationData":[TD([[makeQuery(id+"F1.imprint","IMPRINT",EDGE,{"derivedFrom":subQ2}),-1.0]])]});}
            var Q45;
            {var subQ0=sQuery(id+"F1.wireOp",EDGE,"E132");Q45=makeQuery(id+"F1.imprint","IMPRINT",FACE,{"disambiguationData":[TD([[makeQuery(id+"F1.imprint","IMPRINT",EDGE,{"derivedFrom":subQ0}),1.0]])]});}
            var Q46;
            {var subQ3=sQuery(id+"F1.wireOp",EDGE,"E131.bottom");Q46=makeQuery(id+"F1.imprint","IMPRINT",FACE,{"disambiguationData":[TD([[makeQuery(id+"F1.imprint","IMPRINT",EDGE,{"derivedFrom":subQ3}),1.0]])]});}
            var Q47;
            {var subQ4=sQuery(id+"F1.wireOp",EDGE,"E136.MirrorCS");Q47=makeQuery(id+"F1.imprint","IMPRINT",FACE,{"disambiguationData":[TD([[makeQuery(id+"F1.imprint","IMPRINT",EDGE,{"derivedFrom":subQ4}),-1.0]])]});}
            var Q48;
            {var subQ2=sQuery(id+"F1.wireOp",EDGE,"E138.MirrorCS");Q48=makeQuery(id+"F1.imprint","IMPRINT",FACE,{"disambiguationData":[TD([[makeQuery(id+"F1.imprint","IMPRINT",EDGE,{"derivedFrom":subQ2}),-1.0]])]});}
            var Q49;
            {var subQ3=sQuery(id+"F1.wireOp",EDGE,"c0931354-9de5-41da-893e-8dcd2409041e.MirrorCS");Q49=makeQuery(id+"F1.imprint","IMPRINT",FACE,{"disambiguationData":[TD([[makeQuery(id+"F1.imprint","IMPRINT",EDGE,{"derivedFrom":subQ3}),-1.0]])]});}
            var Q50;
            {var subQ3=sQuery(id+"F1.wireOp",EDGE,"E120.bottom");Q50=makeQuery(id+"F1.imprint","IMPRINT",FACE,{"disambiguationData":[TD([[makeQuery(id+"F1.imprint","IMPRINT",EDGE,{"derivedFrom":subQ3}),1.0]])]});}
            var Q51;
            {var subQ3=sQuery(id+"F1.wireOp",EDGE,"E123.MirrorCS");Q51=makeQuery(id+"F1.imprint","IMPRINT",FACE,{"disambiguationData":[TD([[makeQuery(id+"F1.imprint","IMPRINT",EDGE,{"derivedFrom":subQ3}),-1.0]])]});}
            var Q52;
            {var subQ3=sQuery(id+"F1.wireOp",EDGE,"E107.bottom");Q52=makeQuery(id+"F1.imprint","IMPRINT",FACE,{"disambiguationData":[TD([[makeQuery(id+"F1.imprint","IMPRINT",EDGE,{"derivedFrom":subQ3}),-1.0]])]});}
            var Q53;
            {var subQ3=sQuery(id+"F1.wireOp",EDGE,"E106.bottom");Q53=makeQuery(id+"F1.imprint","IMPRINT",FACE,{"disambiguationData":[TD([[makeQuery(id+"F1.imprint","IMPRINT",EDGE,{"derivedFrom":subQ3}),1.0]])]});}
            var Q54;
            {var subQ0=sQuery(id+"F1.wireOp",EDGE,"E126.MirrorCS");Q54=makeQuery(id+"F1.imprint","IMPRINT",FACE,{"disambiguationData":[TD([[makeQuery(id+"F1.imprint","IMPRINT",EDGE,{"derivedFrom":subQ0}),-1.0]])]});}
            var Q55;
            {var subQ0=sQuery(id+"F1.wireOp",EDGE,"E121");Q55=makeQuery(id+"F1.imprint","IMPRINT",FACE,{"disambiguationData":[TD([[makeQuery(id+"F1.imprint","IMPRINT",EDGE,{"derivedFrom":subQ0}),1.0]])]});}
            var Q56;
            {var subQ2=sQuery(id+"F1.wireOp",EDGE,"E108");Q56=makeQuery(id+"F1.imprint","IMPRINT",FACE,{"disambiguationData":[TD([[makeQuery(id+"F1.imprint","IMPRINT",EDGE,{"derivedFrom":subQ2}),-1.0]])]});}
            var Q57;
            {var subQ2=sQuery(id+"F1.wireOp",EDGE,"E116.MirrorCS");Q57=makeQuery(id+"F1.imprint","IMPRINT",FACE,{"disambiguationData":[TD([[makeQuery(id+"F1.imprint","IMPRINT",EDGE,{"derivedFrom":subQ2}),1.0]])]});}
            var Q58;
            {var subQ2=sQuery(id+"F1.wireOp",EDGE,"E111.MirrorCS");Q58=makeQuery(id+"F1.imprint","IMPRINT",FACE,{"disambiguationData":[TD([[makeQuery(id+"F1.imprint","IMPRINT",EDGE,{"derivedFrom":subQ2}),-1.0]])]});}
            var Q59;
            Q59=makeQuery(id+"F1.imprint","IMPRINT",FACE,{"disambiguationData":[TD([[makeQuery(id+"F1.imprint","IMPRINT",EDGE,{"derivedFrom":sQuery(id+"F1.wireOp",EDGE,"E65")}),1.0]])]});
            var Q60;
            Q60=makeQuery(id+"F1.imprint","IMPRINT",FACE,{"disambiguationData":[TD([[makeQuery(id+"F1.imprint","IMPRINT",EDGE,{"derivedFrom":sQuery(id+"F1.wireOp",EDGE,"E56")}),1.0]])]});
            var Q61;
            Q61=makeQuery(id+"F1.imprint","IMPRINT",FACE,{"disambiguationData":[TD([[makeQuery(id+"F1.imprint","IMPRINT",EDGE,{"derivedFrom":sQuery(id+"F1.wireOp",EDGE,"E47")}),1.0]])]});
            var Q62;
            {var subQ2=sQuery(id+"F1.wireOp",EDGE,"E141.MirrorCS");Q62=makeQuery(id+"F1.imprint","IMPRINT",FACE,{"disambiguationData":[TD([[makeQuery(id+"F1.imprint","IMPRINT",EDGE,{"derivedFrom":subQ2}),1.0]])]});}
            var Q63;
            {var subQ2=sQuery(id+"F1.wireOp",EDGE,"E169.MirrorCS");Q63=makeQuery(id+"F1.imprint","IMPRINT",FACE,{"disambiguationData":[TD([[makeQuery(id+"F1.imprint","IMPRINT",EDGE,{"derivedFrom":subQ2}),-1.0]])]});}
            var Q64;
            {var subQ0=sQuery(id+"F1.wireOp",EDGE,"E186.MirrorCS");Q64=makeQuery(id+"F1.imprint","IMPRINT",FACE,{"disambiguationData":[TD([[makeQuery(id+"F1.imprint","IMPRINT",EDGE,{"derivedFrom":subQ0}),-1.0]])]});}
            var Q65;
            {var subQ0=sQuery(id+"F1.wireOp",EDGE,"E181.MirrorCS");Q65=makeQuery(id+"F1.imprint","IMPRINT",FACE,{"disambiguationData":[TD([[makeQuery(id+"F1.imprint","IMPRINT",EDGE,{"derivedFrom":subQ0}),-1.0]])]});}
            var Q66;
            {var subQ0=sQuery(id+"F1.wireOp",EDGE,"E184.MirrorCS");Q66=makeQuery(id+"F1.imprint","IMPRINT",FACE,{"disambiguationData":[TD([[makeQuery(id+"F1.imprint","IMPRINT",EDGE,{"derivedFrom":subQ0}),-1.0]])]});}
            extrude(context, id + "F2", {"entities" : qUnion([Q0, Q1, Q2, Q3, Q4, Q5, Q6, Q7, Q8, Q9, Q10, Q11, Q12, Q13, Q14, Q15, Q16, Q17, Q18, Q19, Q20, Q21, Q22, Q23, Q24, Q25, Q26, Q27, Q28, Q29, Q30, Q31, Q32, Q33, Q34, Q35, Q36, Q37, Q38, Q39, Q40, Q41, Q42, Q43, Q44, Q45, Q46, Q47, Q48, Q49, Q50, Q51, Q52, Q53, Q54, Q55, Q56, Q57, Q58, Q59, Q60, Q61, Q62, Q63, Q64, Q65, Q66]), "depth" : 2 * mm});
        }
        {
            var Q0;
            Q0=makeQuery(id+"F1.imprint","IMPRINT",FACE,{"disambiguationData":[TD([[makeQuery(id+"F1.imprint","IMPRINT",EDGE,{"derivedFrom":sQuery(id+"F1.wireOp",EDGE,"E45.top")}),1.0]])]});
            extrude(context, id + "F3", {"entities" : qUnion([Q0]), "operationType" : NewBodyOperationType.ADD, "depth" : 11.5 * mm});
        }
        {
            var Q0;
            Q0=qCreatedBy(makeId("Front.planeOp"),FACE);
            var sketch = newSketch(context, id + "F4", { "sketchPlane" : qUnion([Q0])});
            skLineSegment(sketch, "E188", {"start": v(65.8, 0) * mm, "end": v(65.8, 15.48) * mm, "construction": true});
            skLineSegment(sketch, "E189", {"start": v(29.8, 0) * mm, "end": v(29.8, 15.59) * mm, "construction": true});
            skLineSegment(sketch, "E190", {"start": v(-81.75, 0) * mm, "end": v(-81.75, 15.53) * mm, "construction": true});
            skLineSegment(sketch, "E191", {"start": v(-18.9, 15.53) * mm, "end": v(-18.9, 0) * mm, "construction": true});
            skLineSegment(sketch, "E192", {"start": v(-66.9, 0) * mm, "end": v(-66.9, 14.86) * mm, "construction": true});
            skLineSegment(sketch, "E193", {"start": v(70.3, 4) * mm, "end": v(61.31, 4) * mm, "construction": true});
            skLineSegment(sketch, "E194", {"start": v(33.27, 6) * mm, "end": v(25.28, 6) * mm, "construction": true});
            skLineSegment(sketch, "E195", {"start": v(-71.75, 8.5) * mm, "end": v(-5.23, 8.5) * mm, "construction": true});
            skCircle(sketch, "E196", {"center": v(65.8, 4) * mm, "radius": 1.75 * mm});
            skCircle(sketch, "E197", {"center": v(29.8, 6) * mm, "radius": 1.75 * mm});
            skCircle(sketch, "E198", {"center": v(-18.9, 8.5) * mm, "radius": 1.75 * mm});
            skCircle(sketch, "E199", {"center": v(-66.9, 8.5) * mm, "radius": 1.75 * mm});
            skSolve(sketch);
        }
        {
            var Q0;
            Q0=makeQuery(id+"F4.imprint","IMPRINT",FACE,{"disambiguationData":[TD([[makeQuery(id+"F4.imprint","IMPRINT",EDGE,{"derivedFrom":sQuery(id+"F4.wireOp",EDGE,"E198")}),1.0]])]});
            var Q1;
            Q1=makeQuery(id+"F4.imprint","IMPRINT",FACE,{"disambiguationData":[TD([[makeQuery(id+"F4.imprint","IMPRINT",EDGE,{"derivedFrom":sQuery(id+"F4.wireOp",EDGE,"E199")}),1.0]])]});
            var Q2;
            Q2=makeQuery(id+"F4.imprint","IMPRINT",FACE,{"disambiguationData":[TD([[makeQuery(id+"F4.imprint","IMPRINT",EDGE,{"derivedFrom":sQuery(id+"F4.wireOp",EDGE,"E197")}),1.0]])]});
            var Q3;
            Q3=makeQuery(id+"F4.imprint","IMPRINT",FACE,{"disambiguationData":[TD([[makeQuery(id+"F4.imprint","IMPRINT",EDGE,{"derivedFrom":sQuery(id+"F4.wireOp",EDGE,"E196")}),1.0]])]});
            extrude(context, id + "F5", {"entities" : qUnion([Q0, Q1, Q2, Q3]), "operationType" : NewBodyOperationType.REMOVE, "depth" : 19 * mm});
        }
    });
